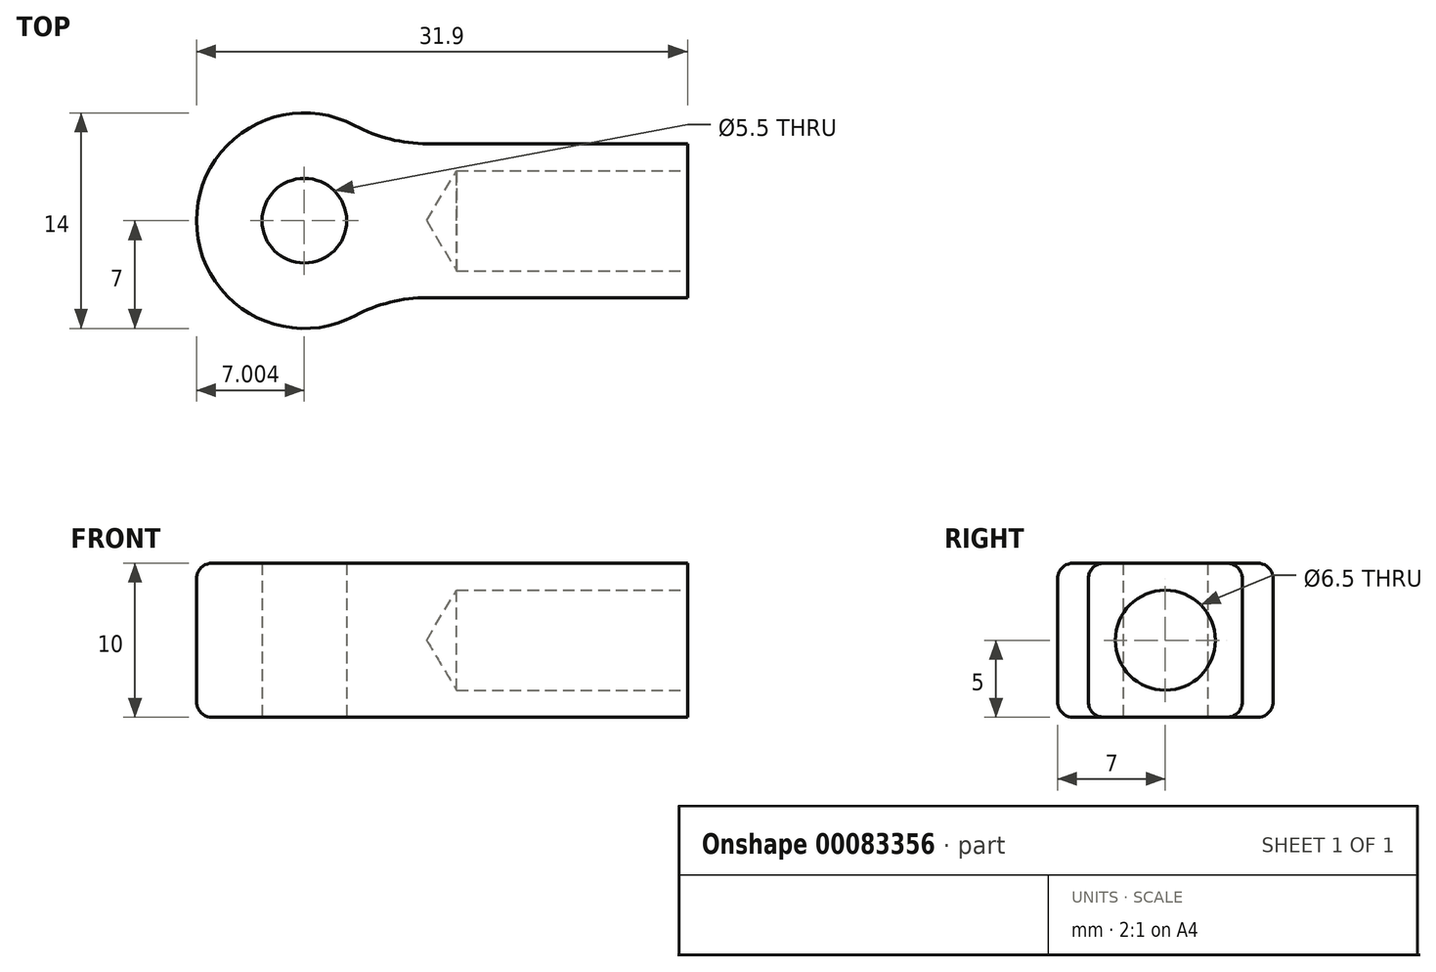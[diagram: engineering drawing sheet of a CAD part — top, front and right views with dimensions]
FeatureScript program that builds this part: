
annotation { "Feature Type Name" : "Feature", "Feature Type Description" : "" }
export const myFeature = defineFeature(function(context is Context, id is Id, definition is map)
    precondition{}
    {
        {
            var Q0;
            Q0=qCreatedBy(makeId("Top.planeOp"),FACE);
            var sketch = newSketch(context, id + "F0", { "sketchPlane" : qUnion([Q0])});
            skLineSegment(sketch, "E0", {"start": v(-7.88, 0) * mm, "end": v(12.12, 0) * mm, "construction": true});
            skCircle(sketch, "E1", {"center": v(-7.88, 0) * mm, "radius": 2.75 * mm});
            skCircle(sketch, "E2", {"center": v(-7.88, 0) * mm, "radius": 7 * mm});
            skLineSegment(sketch, "E3", {"start": v(-2.98, 5) * mm, "end": v(17.02, 5) * mm});
            skLineSegment(sketch, "E4", {"start": v(17.02, -5) * mm, "end": v(-2.98, -5) * mm});
            skLineSegment(sketch, "E5", {"start": v(17.02, -5) * mm, "end": v(17.02, 5) * mm});
            skSolve(sketch);
        }
        {
            var Q0;
            Q0=makeQuery(id+"F0.imprint","IMPRINT",FACE,{"disambiguationData":[TD([[makeQuery(id+"F0.imprint","IMPRINT",EDGE,{"derivedFrom":sQuery(id+"F0.wireOp",EDGE,"E1")}),-1.0]])]});
            var Q1;
            {var subQ0=sQuery(id+"F0.wireOp",EDGE,"E3");Q1=makeQuery(id+"F0.imprint","IMPRINT",FACE,{"disambiguationData":[TD([[makeQuery(id+"F0.imprint","IMPRINT",EDGE,{"derivedFrom":subQ0}),-1.0]])]});}
            var Q2;
            Q2=makeQuery(id+"F0.imprint","IMPRINT",FACE,{"disambiguationData":[TD([[makeQuery(id+"F0.imprint","IMPRINT",EDGE,{"derivedFrom":sQuery(id+"F0.wireOp",EDGE,"EYT0Hesz-W4zW-jKfW-lamI-fLxvZ1qRtDKd")}),-1.0]])]});
            extrude(context, id + "F1", {"entities" : qUnion([Q0, Q1, Q2]), "depth" : 10 * mm});
        }
        {
            var Q0;
            Q0=makeQuery(id+"F1.opExtrude","SWEPT_EDGE",EDGE,{"disambiguationData":[OSD([sQuery(id+"F0.wireOp",EDGE,"E2"),sQuery(id+"F0.wireOp",EDGE,"E3")])]});
            var Q1;
            Q1=makeQuery(id+"F1.opExtrude","SWEPT_EDGE",EDGE,{"disambiguationData":[OSD([sQuery(id+"F0.wireOp",EDGE,"E2"),sQuery(id+"F0.wireOp",EDGE,"E4")])]});
            fillet(context, id + "F2", {"entities" : qUnion([Q0, Q1]), "radius" : 10 * mm, "tangentPropagation" : true, "allowEdgeOverflow" : false});
        }
        {
            var Q0;
            Q0=makeQuery(id+"F1.opExtrude","CAP_EDGE",EDGE,{"disambiguationData":[OSD([sQuery(id+"F0.wireOp",EDGE,"E3")])],"isStart":false});
            var Q1;
            {var subQ0=sQuery(id+"F0.wireOp",EDGE,"E3");var subQ1=sQuery(id+"F0.wireOp",EDGE,"E2");Q1=makeQuery(id+"F2.opFillet","BLEND_EDGE",EDGE,{"blendedFrom":[makeQuery(id+"F1.opExtrude","SWEPT_EDGE",EDGE,{"disambiguationData":[OSD([subQ1,subQ0])]}),makeQuery(id+"F1.opExtrude","CAP_FACE",FACE,{"disambiguationData":[OSD([sQuery(id+"F0.wireOp",EDGE,"E1"),sQuery(id+"F0.wireOp",EDGE,"EYT0Hesz-W4zW-jKfW-lamI-fLxvZ1qRtDKd"),sQuery(id+"F0.wireOp",EDGE,"VOR8jTyN-zS6P-1tWr-jR5d-f18mjQTJMBSX"),subQ1,subQ0,sQuery(id+"F0.wireOp",EDGE,"E4")])],"isStart":false})],"blendedInto":[makeQuery(id+"F1.opExtrude","CAP_FACE",FACE,{"disambiguationData":[OSD([sQuery(id+"F0.wireOp",EDGE,"E1"),sQuery(id+"F0.wireOp",EDGE,"EYT0Hesz-W4zW-jKfW-lamI-fLxvZ1qRtDKd"),sQuery(id+"F0.wireOp",EDGE,"VOR8jTyN-zS6P-1tWr-jR5d-f18mjQTJMBSX"),subQ1,subQ0,sQuery(id+"F0.wireOp",EDGE,"E4")])],"isStart":false})]});}
            var Q2;
            Q2=makeQuery(id+"F1.opExtrude","CAP_EDGE",EDGE,{"disambiguationData":[OSD([sQuery(id+"F0.wireOp",EDGE,"E3")])],"isStart":true});
            fillet(context, id + "F3", {"entities" : qUnion([Q0, Q1, Q2]), "radius" : 1 * mm, "tangentPropagation" : true, "allowEdgeOverflow" : false});
        }
        {
            var Q0;
            Q0=makeQuery(id+"F1.opExtrude","SWEPT_FACE",FACE,{"disambiguationData":[OSD([sQuery(id+"F0.wireOp",EDGE,"E5")])]});
            var sketch = newSketch(context, id + "F4", { "sketchPlane" : qUnion([Q0])});
            skLineSegment(sketch, "E6", {"start": v(0, 10) * mm, "end": v(0, 0) * mm, "construction": true});
            skPoint(sketch, "E7", {"position": v(0, 5) * mm});
            skSolve(sketch);
        }
        {
            var Q0;
            Q0=sQuery(id+"F4.wireOp",VERTEX,"E7");
            var Q1;
            Q1=makeQuery(id+"F1.opExtrude","SWEPT_BODY",BODY,{"disambiguationData":[OSD([sQuery(id+"F0.wireOp",EDGE,"E1"),sQuery(id+"F0.wireOp",EDGE,"E2"),sQuery(id+"F0.wireOp",EDGE,"E3"),sQuery(id+"F0.wireOp",EDGE,"E4"),sQuery(id+"F0.wireOp",EDGE,"E5")])]});
            hole(context, id + "F5", {"style" : HoleStyle.SIMPLE, "endStyle" : HoleEndStyle.BLIND, "holeDiameter" : 6.5 * mm, "holeDepth" : 15 * mm, "locations" : qUnion([Q0]), "scope" : qUnion([Q1])});
        }
    });
